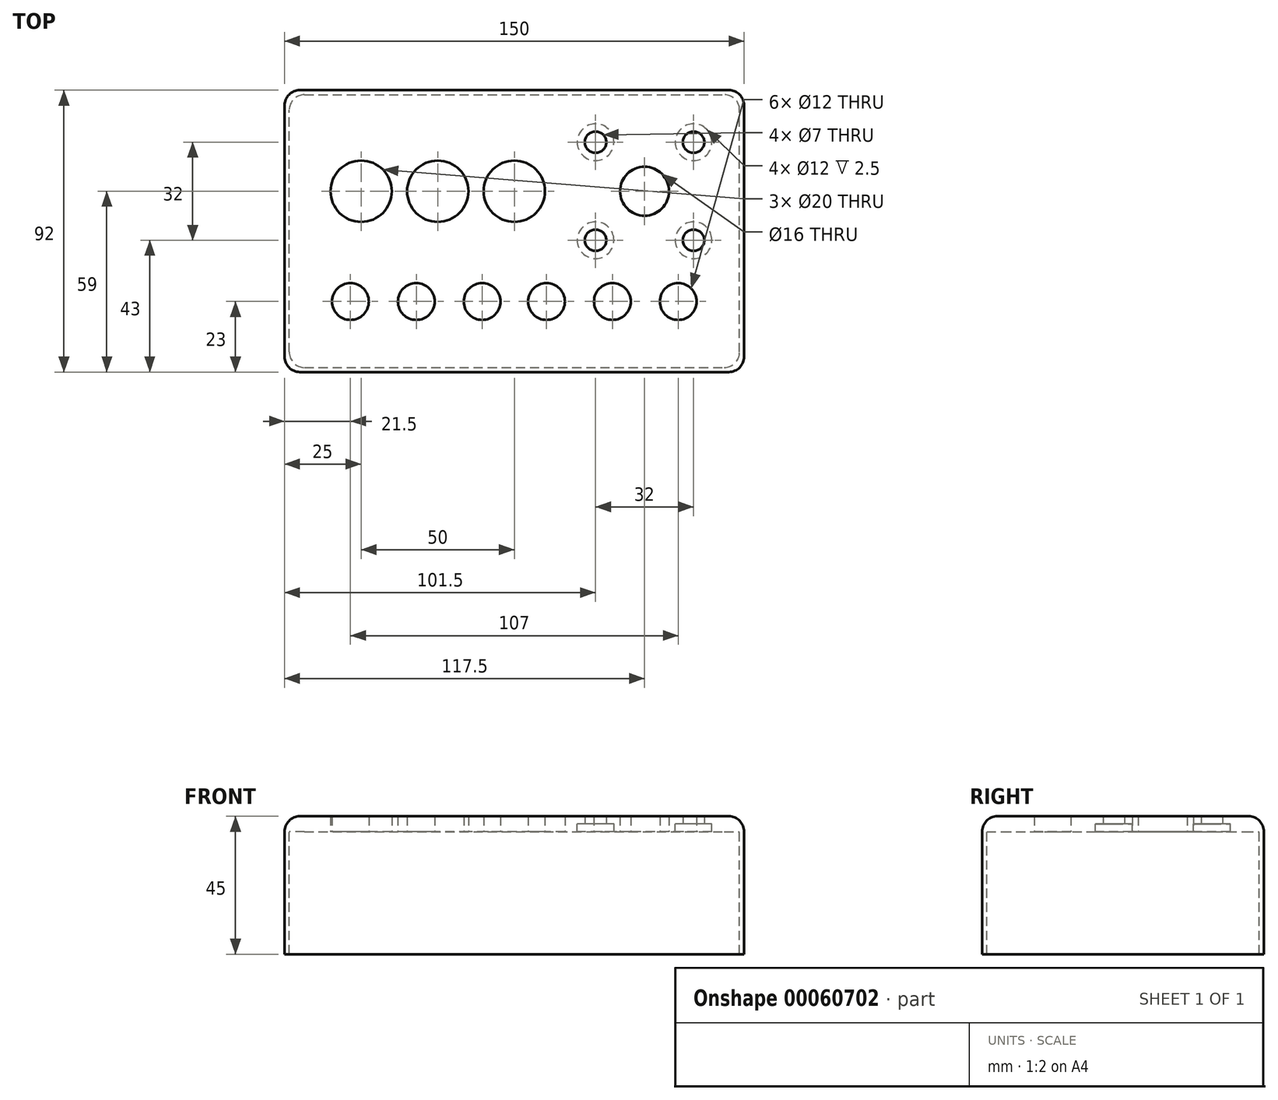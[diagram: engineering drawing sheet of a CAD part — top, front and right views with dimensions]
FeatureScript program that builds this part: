
annotation { "Feature Type Name" : "Feature", "Feature Type Description" : "" }
export const myFeature = defineFeature(function(context is Context, id is Id, definition is map)
    precondition{}
    {
        {
            var Q0;
            Q0=qCreatedBy(makeId("Top.planeOp"),FACE);
            var sketch = newSketch(context, id + "F0", { "sketchPlane" : qUnion([Q0])});
            skLineSegment(sketch, "E0.bottom", {"start": v(0, 0) * mm, "end": v(150, 0) * mm});
            skLineSegment(sketch, "E0.top", {"start": v(0, 92) * mm, "end": v(150, 92) * mm});
            skLineSegment(sketch, "E0.left", {"start": v(0, 0) * mm, "end": v(0, 92) * mm});
            skLineSegment(sketch, "E0.right", {"start": v(150, 0) * mm, "end": v(150, 92) * mm});
            skCircle(sketch, "E1", {"center": v(25, 59) * mm, "radius": 10 * mm});
            skCircle(sketch, "E2", {"center": v(50, 59) * mm, "radius": 10 * mm});
            skCircle(sketch, "E3", {"center": v(75, 59) * mm, "radius": 10 * mm});
            skCircle(sketch, "E4", {"center": v(21.5, 23) * mm, "radius": 6 * mm});
            skCircle(sketch, "E5", {"center": v(43, 23) * mm, "radius": 6 * mm});
            skCircle(sketch, "E6", {"center": v(64.5, 23) * mm, "radius": 6 * mm});
            skCircle(sketch, "E7", {"center": v(85.5, 23) * mm, "radius": 6 * mm});
            skCircle(sketch, "E8", {"center": v(107, 23) * mm, "radius": 6 * mm});
            skCircle(sketch, "E9", {"center": v(128.5, 23) * mm, "radius": 6 * mm});
            skCircle(sketch, "E10", {"center": v(117.5, 59) * mm, "radius": 8 * mm});
            skCircle(sketch, "E11", {"center": v(101.5, 75) * mm, "radius": 3.5 * mm});
            skCircle(sketch, "E12", {"center": v(133.5, 75) * mm, "radius": 3.5 * mm});
            skCircle(sketch, "E13", {"center": v(133.5, 43) * mm, "radius": 3.5 * mm});
            skCircle(sketch, "E14", {"center": v(101.5, 43) * mm, "radius": 3.5 * mm});
            skSolve(sketch);
        }
        {
            var Q0;
            Q0=makeQuery(id+"F0.imprint","IMPRINT",FACE,{"disambiguationData":[TD([[makeQuery(id+"F0.imprint","IMPRINT",EDGE,{"derivedFrom":sQuery(id+"F0.wireOp",EDGE,"E0.bottom")}),1.0]])]});
            extrude(context, id + "F1", {"entities" : qUnion([Q0]), "depth" : 2.5 * mm});
        }
        {
            var Q0;
            Q0=makeQuery(id+"F0.imprint","IMPRINT",FACE,{"disambiguationData":[TD([[makeQuery(id+"F0.imprint","IMPRINT",EDGE,{"derivedFrom":sQuery(id+"F0.wireOp",EDGE,"E0.bottom")}),1.0]])]});
            var sketch = newSketch(context, id + "F2", { "sketchPlane" : qUnion([Q0])});
            skLineSegment(sketch, "E15.0.0", {"start": v(0, 92) * mm, "end": v(0, 0) * mm});
            skLineSegment(sketch, "E15.0.1", {"start": v(0, 0) * mm, "end": v(150, 0) * mm});
            skLineSegment(sketch, "E15.0.2", {"start": v(150, 0) * mm, "end": v(150, 92) * mm});
            skLineSegment(sketch, "E15.0.3", {"start": v(150, 92) * mm, "end": v(0, 92) * mm});
            skLineSegment(sketch, "E16.top", {"start": v(0, 92) * mm, "end": v(150, 92) * mm});
            skLineSegment(sketch, "E16.left", {"start": v(0, 0) * mm, "end": v(0, 92) * mm});
            skCircle(sketch, "E17", {"center": v(25, 59) * mm, "radius": 10 * mm});
            skCircle(sketch, "E18", {"center": v(50, 59) * mm, "radius": 10 * mm});
            skCircle(sketch, "E19", {"center": v(75, 59) * mm, "radius": 10 * mm});
            skCircle(sketch, "E20", {"center": v(21.5, 23) * mm, "radius": 6 * mm});
            skCircle(sketch, "E21", {"center": v(43, 23) * mm, "radius": 6 * mm});
            skCircle(sketch, "E22", {"center": v(64.5, 23) * mm, "radius": 6 * mm});
            skCircle(sketch, "E23", {"center": v(85.5, 23) * mm, "radius": 6 * mm});
            skCircle(sketch, "E24", {"center": v(107, 23) * mm, "radius": 6 * mm});
            skCircle(sketch, "E25", {"center": v(128.5, 23) * mm, "radius": 6 * mm});
            skCircle(sketch, "E26", {"center": v(117.5, 59) * mm, "radius": 8 * mm});
            skCircle(sketch, "E27", {"center": v(101.5, 75) * mm, "radius": 6 * mm});
            skCircle(sketch, "E28", {"center": v(133.5, 75) * mm, "radius": 6 * mm});
            skCircle(sketch, "E29", {"center": v(133.5, 43) * mm, "radius": 6 * mm});
            skCircle(sketch, "E30", {"center": v(101.5, 43) * mm, "radius": 6 * mm});
            skSolve(sketch);
        }
        {
            var Q0;
            Q0=makeQuery(id+"F2.imprint","IMPRINT",FACE,{"disambiguationData":[TD([[makeQuery(id+"F2.imprint","IMPRINT",EDGE,{"derivedFrom":sQuery(id+"F2.wireOp",EDGE,"E15.0.1")}),1.0]])]});
            extrude(context, id + "F3", {"entities" : qUnion([Q0]), "operationType" : NewBodyOperationType.ADD, "oppositeDirection" : true, "depth" : 2.5 * mm});
        }
        {
            var Q0;
            Q0=makeQuery(id+"F3.opExtrude","CAP_FACE",FACE,{"disambiguationData":[OSD([sQuery(id+"F2.wireOp",EDGE,"E15.0.1"),sQuery(id+"F2.wireOp",EDGE,"E16.top"),sQuery(id+"F2.wireOp",EDGE,"E16.left"),sQuery(id+"F2.wireOp",EDGE,"E15.0.2"),sQuery(id+"F2.wireOp",EDGE,"E17"),sQuery(id+"F2.wireOp",EDGE,"E18"),sQuery(id+"F2.wireOp",EDGE,"E19"),sQuery(id+"F2.wireOp",EDGE,"E20"),sQuery(id+"F2.wireOp",EDGE,"E21"),sQuery(id+"F2.wireOp",EDGE,"E22"),sQuery(id+"F2.wireOp",EDGE,"E23"),sQuery(id+"F2.wireOp",EDGE,"E24"),sQuery(id+"F2.wireOp",EDGE,"E25"),sQuery(id+"F2.wireOp",EDGE,"E26"),sQuery(id+"F2.wireOp",EDGE,"E27"),sQuery(id+"F2.wireOp",EDGE,"E28"),sQuery(id+"F2.wireOp",EDGE,"E29"),sQuery(id+"F2.wireOp",EDGE,"E30")])],"isStart":false});
            var sketch = newSketch(context, id + "F4", { "sketchPlane" : qUnion([Q0])});
            skLineSegment(sketch, "E31.bottom", {"start": v(0, 0) * mm, "end": v(150, 0) * mm});
            skLineSegment(sketch, "E31.top", {"start": v(0, -92) * mm, "end": v(150, -92) * mm});
            skLineSegment(sketch, "E31.left", {"start": v(0, 0) * mm, "end": v(0, -92) * mm});
            skLineSegment(sketch, "E31.right", {"start": v(150, 0) * mm, "end": v(150, -92) * mm});
            skLineSegment(sketch, "E32.bottom", {"start": v(6.5, -1.5) * mm, "end": v(143.5, -1.5) * mm});
            skLineSegment(sketch, "E32.top", {"start": v(6.5, -90.5) * mm, "end": v(143.5, -90.5) * mm});
            skLineSegment(sketch, "E32.left", {"start": v(1.5, -6.5) * mm, "end": v(1.5, -85.5) * mm});
            skLineSegment(sketch, "E32.right", {"start": v(148.5, -6.5) * mm, "end": v(148.5, -85.5) * mm});
            skPoint(sketch, "E33.visualSharp", {"position": v(1.5, -1.5) * mm});
            skArc(sketch, "E33.filletArc", {"start": v(6.5, -1.5) * mm, "mid": v(2.96, -2.96) * mm, "end": v(1.5, -6.5) * mm});
            skPoint(sketch, "E34.visualSharp", {"position": v(148.5, -1.5) * mm});
            skArc(sketch, "E34.filletArc", {"start": v(148.5, -6.5) * mm, "mid": v(147.04, -2.96) * mm, "end": v(143.5, -1.5) * mm});
            skPoint(sketch, "E35.visualSharp", {"position": v(1.5, -90.5) * mm});
            skArc(sketch, "E35.filletArc", {"start": v(1.5, -85.5) * mm, "mid": v(2.96, -89.04) * mm, "end": v(6.5, -90.5) * mm});
            skPoint(sketch, "E36.visualSharp", {"position": v(148.5, -90.5) * mm});
            skArc(sketch, "E36.filletArc", {"start": v(143.5, -90.5) * mm, "mid": v(147.04, -89.04) * mm, "end": v(148.5, -85.5) * mm});
            skSolve(sketch);
        }
        {
            var Q0;
            Q0=makeQuery(id+"F4.imprint","IMPRINT",FACE,{"disambiguationData":[TD([[makeQuery(id+"F4.imprint","IMPRINT",EDGE,{"derivedFrom":sQuery(id+"F4.wireOp",EDGE,"E31.bottom")}),-1.0]])]});
            extrude(context, id + "F5", {"entities" : qUnion([Q0]), "operationType" : NewBodyOperationType.ADD, "depth" : 40 * mm});
        }
        {
            var Q0;
            Q0=makeQuery(id+"F1.opExtrude","CAP_EDGE",EDGE,{"disambiguationData":[OSD([sQuery(id+"F0.wireOp",EDGE,"E0.bottom")])],"isStart":false});
            var Q1;
            Q1=makeQuery(id+"F5.boolean.opBoolean","MERGE",EDGE,{"derivedFrom":[makeQuery(id+"F3.boolean.opBoolean","MERGE",EDGE,{"derivedFrom":[makeQuery(id+"F1.opExtrude","SWEPT_EDGE",EDGE,{"disambiguationData":[OSD([sQuery(id+"F0.wireOp",EDGE,"E0.bottom"),sQuery(id+"F0.wireOp",EDGE,"E0.right")])]}),makeQuery(id+"F3.opExtrude","SWEPT_EDGE",EDGE,{"disambiguationData":[OSD([sQuery(id+"F2.wireOp",EDGE,"E15.0.1"),sQuery(id+"F2.wireOp",EDGE,"E15.0.2")])]})]}),makeQuery(id+"F5.opExtrude","SWEPT_EDGE",EDGE,{"disambiguationData":[OSD([sQuery(id+"F4.wireOp",EDGE,"E31.bottom"),sQuery(id+"F4.wireOp",EDGE,"E31.right")])]})]});
            var Q2;
            Q2=makeQuery(id+"F1.opExtrude","CAP_EDGE",EDGE,{"disambiguationData":[OSD([sQuery(id+"F0.wireOp",EDGE,"E0.right")])],"isStart":false});
            var Q3;
            Q3=makeQuery(id+"F5.boolean.opBoolean","MERGE",EDGE,{"derivedFrom":[makeQuery(id+"F3.boolean.opBoolean","MERGE",EDGE,{"derivedFrom":[makeQuery(id+"F1.opExtrude","SWEPT_EDGE",EDGE,{"disambiguationData":[OSD([sQuery(id+"F0.wireOp",EDGE,"E0.top"),sQuery(id+"F0.wireOp",EDGE,"E0.right")])]}),makeQuery(id+"F3.opExtrude","SWEPT_EDGE",EDGE,{"disambiguationData":[OSD([sQuery(id+"F2.wireOp",EDGE,"E16.top"),sQuery(id+"F2.wireOp",EDGE,"E15.0.2")])]})]}),makeQuery(id+"F5.opExtrude","SWEPT_EDGE",EDGE,{"disambiguationData":[OSD([sQuery(id+"F4.wireOp",EDGE,"E31.top"),sQuery(id+"F4.wireOp",EDGE,"E31.right")])]})]});
            var Q4;
            Q4=makeQuery(id+"F1.opExtrude","CAP_EDGE",EDGE,{"disambiguationData":[OSD([sQuery(id+"F0.wireOp",EDGE,"E0.top")])],"isStart":false});
            var Q5;
            Q5=makeQuery(id+"F1.opExtrude","CAP_EDGE",EDGE,{"disambiguationData":[OSD([sQuery(id+"F0.wireOp",EDGE,"E0.left")])],"isStart":false});
            var Q6;
            Q6=makeQuery(id+"F5.boolean.opBoolean","MERGE",EDGE,{"derivedFrom":[makeQuery(id+"F3.boolean.opBoolean","MERGE",EDGE,{"derivedFrom":[makeQuery(id+"F1.opExtrude","SWEPT_EDGE",EDGE,{"disambiguationData":[OSD([sQuery(id+"F0.wireOp",EDGE,"E0.top"),sQuery(id+"F0.wireOp",EDGE,"E0.left")])]}),makeQuery(id+"F3.opExtrude","SWEPT_EDGE",EDGE,{"disambiguationData":[OSD([sQuery(id+"F2.wireOp",EDGE,"E16.top"),sQuery(id+"F2.wireOp",EDGE,"E16.left")])]})]}),makeQuery(id+"F5.opExtrude","SWEPT_EDGE",EDGE,{"disambiguationData":[OSD([sQuery(id+"F4.wireOp",EDGE,"E31.top"),sQuery(id+"F4.wireOp",EDGE,"E31.left")])]})]});
            var Q7;
            Q7=makeQuery(id+"F5.boolean.opBoolean","MERGE",EDGE,{"derivedFrom":[makeQuery(id+"F3.boolean.opBoolean","MERGE",EDGE,{"derivedFrom":[makeQuery(id+"F1.opExtrude","SWEPT_EDGE",EDGE,{"disambiguationData":[OSD([sQuery(id+"F0.wireOp",EDGE,"E0.bottom"),sQuery(id+"F0.wireOp",EDGE,"E0.left")])]}),makeQuery(id+"F3.opExtrude","SWEPT_EDGE",EDGE,{"disambiguationData":[OSD([sQuery(id+"F2.wireOp",EDGE,"E15.0.1"),sQuery(id+"F2.wireOp",EDGE,"E16.left")])]})]}),makeQuery(id+"F5.opExtrude","SWEPT_EDGE",EDGE,{"disambiguationData":[OSD([sQuery(id+"F4.wireOp",EDGE,"E31.bottom"),sQuery(id+"F4.wireOp",EDGE,"E31.left")])]})]});
            fillet(context, id + "F6", {"entities" : qUnion([Q0, Q1, Q2, Q3, Q4, Q5, Q6, Q7]), "radius" : 5 * mm, "tangentPropagation" : true, "allowEdgeOverflow" : false});
        }
    });
